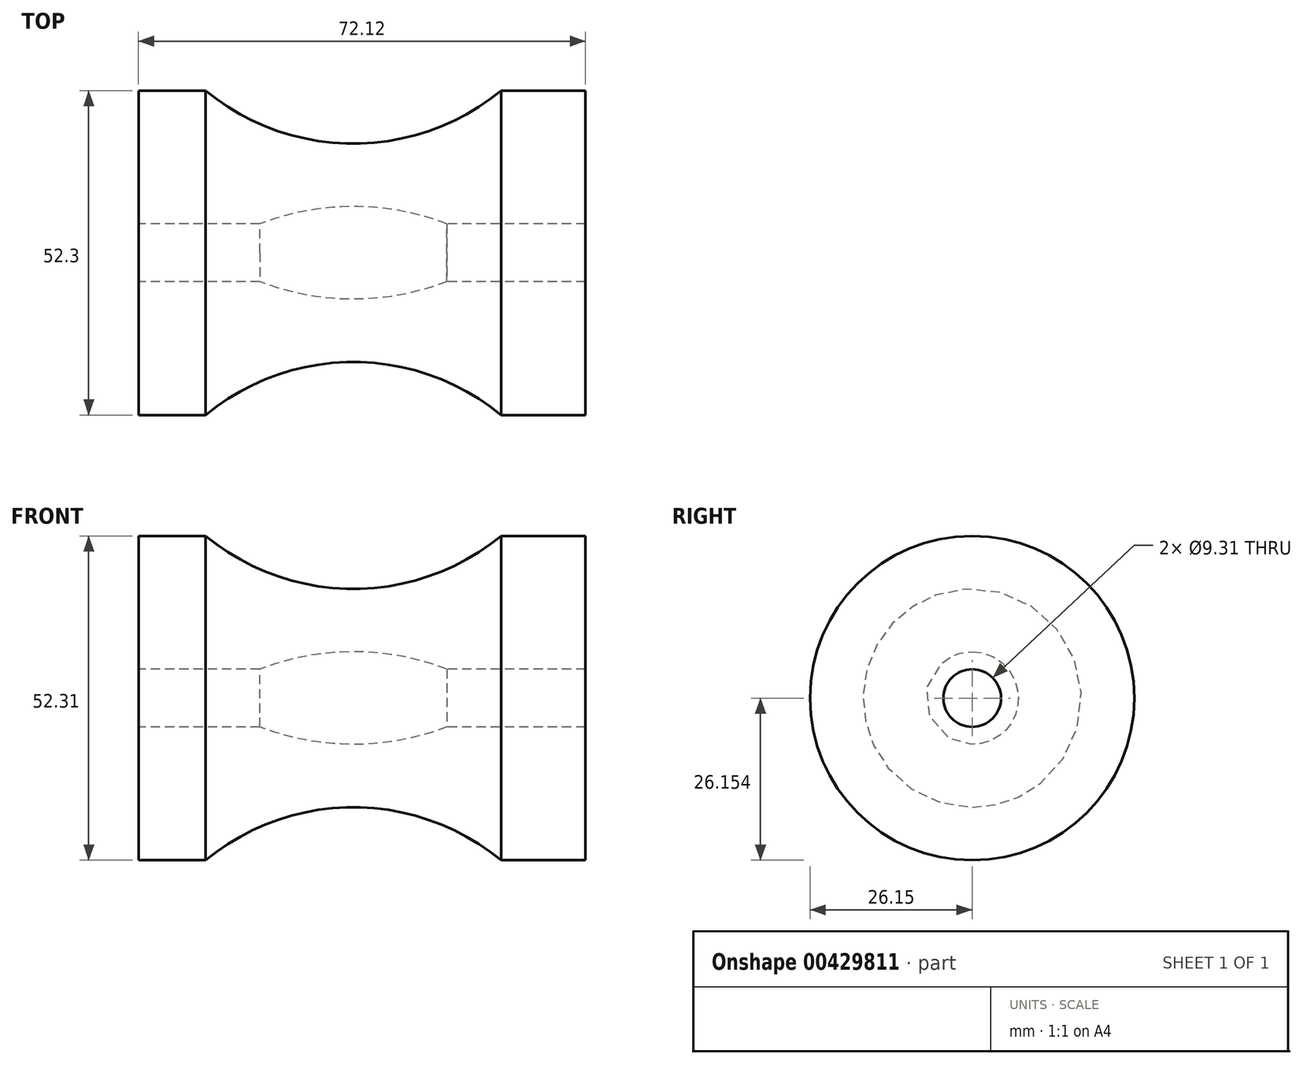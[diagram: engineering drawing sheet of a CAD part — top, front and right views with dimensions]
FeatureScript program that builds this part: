
annotation { "Feature Type Name" : "Feature", "Feature Type Description" : "" }
export const myFeature = defineFeature(function(context is Context, id is Id, definition is map)
    precondition{}
    {
        {
            var Q0;
            Q0=qCreatedBy(makeId("Front.planeOp"),FACE);
            var sketch = newSketch(context, id + "F0", { "sketchPlane" : qUnion([Q0])});
            skLineSegment(sketch, "E0.bottom", {"start": v(0, 0) * mm, "end": v(-13.62, 0) * mm});
            skLineSegment(sketch, "E0.top", {"start": v(0, 26.15) * mm, "end": v(-13.62, 26.15) * mm});
            skLineSegment(sketch, "E0.left", {"start": v(0, 0) * mm, "end": v(0, 26.15) * mm});
            skLineSegment(sketch, "E0.right", {"start": v(-72.12, 0) * mm, "end": v(-72.12, 26.15) * mm});
            skArc(sketch, "E1", {"start": v(-61.28, 26.15) * mm, "mid": v(-37.45, 18.68) * mm, "end": v(-13.62, 26.15) * mm});
            skArc(sketch, "E2", {"start": v(-13.62, 0) * mm, "mid": v(-37.45, 8.54) * mm, "end": v(-61.28, 0) * mm});
            skLineSegment(sketch, "E3.trimOffspring", {"start": v(-61.28, 26.15) * mm, "end": v(-72.12, 26.15) * mm});
            skLineSegment(sketch, "E4.trimOffspring", {"start": v(-61.28, 0) * mm, "end": v(-72.12, 0) * mm});
            skSolve(sketch);
        }
        {
            var Q0;
            Q0=makeQuery(id+"F0.imprint","IMPRINT",FACE,{"disambiguationData":[TD([[makeQuery(id+"F0.imprint","IMPRINT",EDGE,{"derivedFrom":sQuery(id+"F0.wireOp",EDGE,"E0.bottom")}),-1.0]])]});
            var Q1;
            Q1=sQuery(id+"F0.wireOp",EDGE,"E0.top");
            revolve(context, id + "F1", {"entities" : qUnion([Q0]), "axis" : qUnion([Q1]), "revolveType" : RevolveType.FULL});
        }
        {
            var Q0;
            Q0=makeQuery(id+"F1.opRevolve","SWEPT_FACE",FACE,{"disambiguationData":[OSD([sQuery(id+"F0.wireOp",EDGE,"E0.right")])]});
            var sketch = newSketch(context, id + "F2", { "sketchPlane" : qUnion([Q0])});
            skCircle(sketch, "E5", {"center": v(0, 26.15) * mm, "radius": 4.65 * mm});
            skSolve(sketch);
        }
        {
            var Q0;
            Q0 = qSketchRegion(id + "F2", true);
            extrude(context, id + "F3", {"entities" : qUnion([Q0]), "operationType" : NewBodyOperationType.ADD, "depth" : 25.4 * mm});
        }
        {
            var Q0;
            Q0=makeQuery(id+"F3.opExtrude","CAP_FACE",FACE,{"disambiguationData":[OSD([sQuery(id+"F2.wireOp",EDGE,"E5")])],"isStart":false});
            extrude(context, id + "F4", {"entities" : qUnion([Q0]), "operationType" : NewBodyOperationType.REMOVE, "endBound" : BoundingType.THROUGH_ALL, "oppositeDirection" : true, "depth" : 25.4 * mm});
        }
    });
